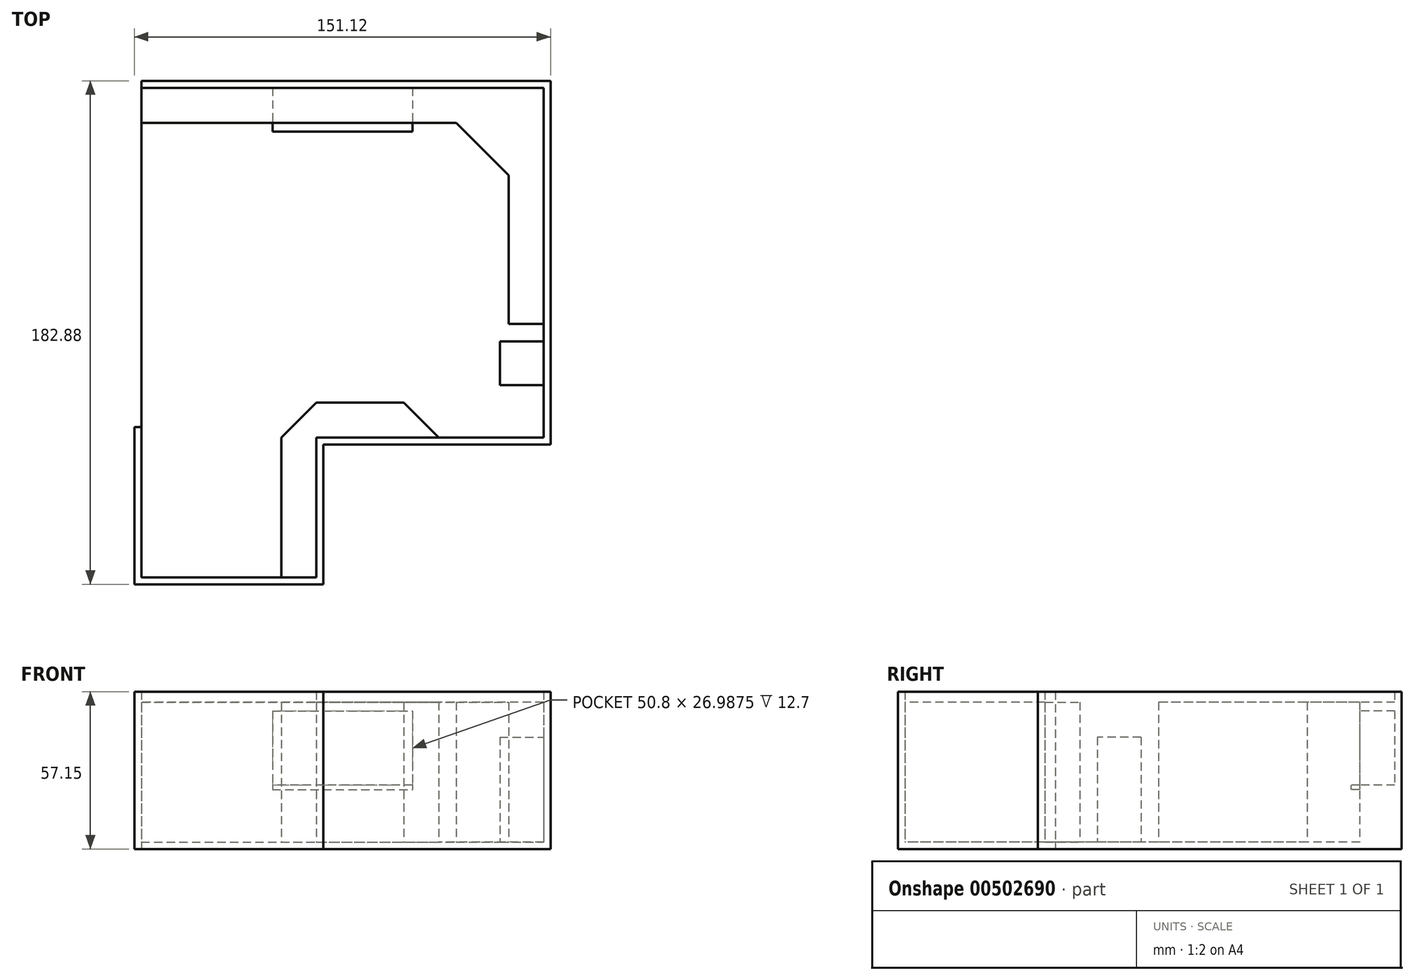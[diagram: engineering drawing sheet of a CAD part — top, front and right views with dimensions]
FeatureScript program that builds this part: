
annotation { "Feature Type Name" : "Feature", "Feature Type Description" : "" }
export const myFeature = defineFeature(function(context is Context, id is Id, definition is map)
    precondition{}
    {
        {
            var Q0;
            Q0=qCreatedBy(makeId("Top.planeOp"),FACE);
            var sketch = newSketch(context, id + "F0", { "sketchPlane" : qUnion([Q0])});
            skLineSegment(sketch, "E0.bottom", {"start": v(73.02, 63.5) * mm, "end": v(-73.03, 63.5) * mm});
            skLineSegment(sketch, "E0.top", {"start": v(73.03, -63.5) * mm, "end": v(-73.02, -63.5) * mm});
            skLineSegment(sketch, "E0.left", {"start": v(73.02, 63.5) * mm, "end": v(73.03, -63.5) * mm});
            skLineSegment(sketch, "E0.right", {"start": v(-73.03, 63.5) * mm, "end": v(-73.02, -63.5) * mm});
            skPoint(sketch, "E0.middle", {"position": v(0, 0) * mm});
            skSolve(sketch);
        }
        {
            var Q0;
            Q0=makeQuery(id+"F0.imprint","IMPRINT",FACE,{"disambiguationData":[TD([[makeQuery(id+"F0.imprint","IMPRINT",EDGE,{"derivedFrom":sQuery(id+"F0.wireOp",EDGE,"E0.bottom")}),1.0]])]});
            extrude(context, id + "F1", {"entities" : qUnion([Q0]), "depth" : 2.54 * mm});
        }
        {
            var Q0;
            Q0=makeQuery(id+"F1.opExtrude","CAP_FACE",FACE,{"disambiguationData":[OSD([sQuery(id+"F0.wireOp",EDGE,"E0.bottom"),sQuery(id+"F0.wireOp",EDGE,"E0.top"),sQuery(id+"F0.wireOp",EDGE,"E0.left"),sQuery(id+"F0.wireOp",EDGE,"E0.right")])],"isStart":false});
            var sketch = newSketch(context, id + "F2", { "sketchPlane" : qUnion([Q0])});
            skLineSegment(sketch, "E1.bottom", {"start": v(-73.03, 63.5) * mm, "end": v(73.03, 63.5) * mm});
            skLineSegment(sketch, "E1.top", {"start": v(-73.03, 50.8) * mm, "end": v(73.03, 50.8) * mm});
            skLineSegment(sketch, "E1.left", {"start": v(-73.03, 63.5) * mm, "end": v(-73.03, 50.8) * mm});
            skLineSegment(sketch, "E1.right", {"start": v(73.02, 63.5) * mm, "end": v(73.02, 50.8) * mm});
            skSolve(sketch);
        }
        {
            var Q0;
            Q0=makeQuery(id+"F2.imprint","IMPRINT",FACE,{"disambiguationData":[TD([[makeQuery(id+"F2.imprint","IMPRINT",EDGE,{"derivedFrom":sQuery(id+"F2.wireOp",EDGE,"E1.bottom")}),1.0]])]});
            extrude(context, id + "F3", {"entities" : qUnion([Q0]), "operationType" : NewBodyOperationType.ADD, "depth" : 50.8 * mm});
        }
        {
            var Q0;
            Q0=makeQuery(id+"F1.opExtrude","CAP_FACE",FACE,{"disambiguationData":[OSD([sQuery(id+"F0.wireOp",EDGE,"E0.bottom"),sQuery(id+"F0.wireOp",EDGE,"E0.top"),sQuery(id+"F0.wireOp",EDGE,"E0.left"),sQuery(id+"F0.wireOp",EDGE,"E0.right")])],"isStart":false});
            var sketch = newSketch(context, id + "F4", { "sketchPlane" : qUnion([Q0])});
            skLineSegment(sketch, "E2.bottom", {"start": v(57.15, -28.58) * mm, "end": v(73.03, -28.58) * mm});
            skLineSegment(sketch, "E2.top", {"start": v(57.15, -44.45) * mm, "end": v(73.03, -44.45) * mm});
            skLineSegment(sketch, "E2.left", {"start": v(57.15, -28.58) * mm, "end": v(57.15, -44.45) * mm});
            skLineSegment(sketch, "E2.right", {"start": v(73.03, -28.58) * mm, "end": v(73.03, -44.45) * mm});
            skSolve(sketch);
        }
        {
            var Q0;
            Q0=makeQuery(id+"F3.opExtrude","SWEPT_FACE",FACE,{"disambiguationData":[OSD([sQuery(id+"F2.wireOp",EDGE,"E1.top")])]});
            var sketch = newSketch(context, id + "F5", { "sketchPlane" : qUnion([Q0])});
            skLineSegment(sketch, "E3.bottom", {"start": v(-25.4, 50.17) * mm, "end": v(25.4, 50.17) * mm});
            skLineSegment(sketch, "E3.top", {"start": v(-25.4, 21.59) * mm, "end": v(25.4, 21.59) * mm});
            skLineSegment(sketch, "E3.left", {"start": v(-25.4, 50.17) * mm, "end": v(-25.4, 21.59) * mm});
            skLineSegment(sketch, "E3.right", {"start": v(25.4, 50.17) * mm, "end": v(25.4, 21.59) * mm});
            skSolve(sketch);
        }
        {
            var Q0;
            Q0=makeQuery(id+"F5.imprint","IMPRINT",FACE,{"disambiguationData":[TD([[makeQuery(id+"F5.imprint","IMPRINT",EDGE,{"derivedFrom":sQuery(id+"F5.wireOp",EDGE,"E3.bottom")}),-1.0]])]});
            extrude(context, id + "F6", {"entities" : qUnion([Q0]), "operationType" : NewBodyOperationType.REMOVE, "oppositeDirection" : true, "depth" : 12.7 * mm});
        }
        {
            var Q0;
            Q0=makeQuery(id+"F6.boolean.opBoolean","COPY",FACE,{"derivedFrom":makeQuery(id+"F6.opExtrude","SWEPT_FACE",FACE,{"disambiguationData":[OSD([sQuery(id+"F5.wireOp",EDGE,"E3.top")])]})});
            var sketch = newSketch(context, id + "F7", { "sketchPlane" : qUnion([Q0])});
            skLineSegment(sketch, "E4.bottom", {"start": v(25.4, 63.5) * mm, "end": v(-25.4, 63.5) * mm});
            skLineSegment(sketch, "E4.top", {"start": v(25.4, 47.63) * mm, "end": v(-25.4, 47.63) * mm});
            skLineSegment(sketch, "E4.left", {"start": v(25.4, 63.5) * mm, "end": v(25.4, 47.63) * mm});
            skLineSegment(sketch, "E4.right", {"start": v(-25.4, 63.5) * mm, "end": v(-25.4, 47.63) * mm});
            skSolve(sketch);
        }
        {
            var Q0;
            {var subQ0=sQuery(id+"F7.wireOp",EDGE,"E4.top");Q0=makeQuery(id+"F7.imprint","IMPRINT",FACE,{"disambiguationData":[TD([[makeQuery(id+"F7.imprint","IMPRINT",EDGE,{"derivedFrom":subQ0}),-1.0]])]});}
            var Q1;
            {var subQ0=sQuery(id+"F7.wireOp",EDGE,"E4.bottom");Q1=makeQuery(id+"F7.imprint","IMPRINT",FACE,{"disambiguationData":[TD([[makeQuery(id+"F7.imprint","IMPRINT",EDGE,{"derivedFrom":subQ0}),-1.0]])]});}
            extrude(context, id + "F8", {"entities" : qUnion([Q0, Q1]), "operationType" : NewBodyOperationType.ADD, "depth" : 1.59 * mm});
        }
        {
            var Q0;
            Q0=qCreatedBy(makeId("Top.planeOp"),FACE);
            var sketch = newSketch(context, id + "F9", { "sketchPlane" : qUnion([Q0])});
            skLineSegment(sketch, "E5.bottom", {"start": v(-73.02, -63.5) * mm, "end": v(-9.52, -63.5) * mm});
            skLineSegment(sketch, "E5.top", {"start": v(-73.02, -114.3) * mm, "end": v(-9.52, -114.3) * mm});
            skLineSegment(sketch, "E5.left", {"start": v(-73.02, -63.5) * mm, "end": v(-73.02, -114.3) * mm});
            skLineSegment(sketch, "E5.right", {"start": v(-9.52, -63.5) * mm, "end": v(-9.52, -114.3) * mm});
            skSolve(sketch);
        }
        {
            var Q0;
            Q0=makeQuery(id+"F9.imprint","IMPRINT",FACE,{"disambiguationData":[TD([[makeQuery(id+"F9.imprint","IMPRINT",EDGE,{"derivedFrom":sQuery(id+"F9.wireOp",EDGE,"E5.bottom")}),-1.0]])]});
            extrude(context, id + "F10", {"entities" : qUnion([Q0]), "operationType" : NewBodyOperationType.ADD, "depth" : 2.54 * mm});
        }
        {
            var Q0;
            Q0=makeQuery(id+"F10.boolean.opBoolean","MERGE",FACE,{"derivedFrom":[makeQuery(id+"F1.opExtrude","CAP_FACE",FACE,{"disambiguationData":[OSD([sQuery(id+"F0.wireOp",EDGE,"E0.bottom"),sQuery(id+"F0.wireOp",EDGE,"E0.top"),sQuery(id+"F0.wireOp",EDGE,"E0.left"),sQuery(id+"F0.wireOp",EDGE,"E0.right")])],"isStart":false}),makeQuery(id+"F10.opExtrude","CAP_FACE",FACE,{"disambiguationData":[OSD([sQuery(id+"F9.wireOp",EDGE,"E5.bottom"),sQuery(id+"F9.wireOp",EDGE,"E5.top"),sQuery(id+"F9.wireOp",EDGE,"E5.left"),sQuery(id+"F9.wireOp",EDGE,"E5.right")])],"isStart":false})]});
            var sketch = newSketch(context, id + "F11", { "sketchPlane" : qUnion([Q0])});
            skLineSegment(sketch, "E6.bottom", {"start": v(73.02, 50.8) * mm, "end": v(60.32, 50.8) * mm});
            skLineSegment(sketch, "E6.top", {"start": v(73.02, -22.23) * mm, "end": v(60.33, -22.23) * mm});
            skLineSegment(sketch, "E6.left", {"start": v(73.02, 50.8) * mm, "end": v(73.02, -22.23) * mm});
            skLineSegment(sketch, "E6.right", {"start": v(60.32, 50.8) * mm, "end": v(60.33, -22.23) * mm});
            skSolve(sketch);
        }
        {
            var Q0;
            Q0 = qSketchRegion(id + "F11", true);
            extrude(context, id + "F12", {"entities" : qUnion([Q0]), "operationType" : NewBodyOperationType.ADD, "depth" : 50.8 * mm});
        }
        {
            var Q0;
            Q0=qCreatedBy(makeId("Top.planeOp"),FACE);
            var sketch = newSketch(context, id + "F13", { "sketchPlane" : qUnion([Q0])});
            skLineSegment(sketch, "E7.bottom", {"start": v(-73.03, 63.5) * mm, "end": v(75.57, 63.5) * mm});
            skLineSegment(sketch, "E7.top", {"start": v(-73.03, 66.04) * mm, "end": v(75.57, 66.04) * mm});
            skLineSegment(sketch, "E7.left", {"start": v(-73.03, 63.5) * mm, "end": v(-73.03, 66.04) * mm});
            skLineSegment(sketch, "E7.right", {"start": v(75.57, 63.5) * mm, "end": v(75.57, 66.04) * mm});
            skSolve(sketch);
        }
        {
            var Q0;
            Q0=qCreatedBy(makeId("Top.planeOp"),FACE);
            var sketch = newSketch(context, id + "F14", { "sketchPlane" : qUnion([Q0])});
            skLineSegment(sketch, "E8.bottom", {"start": v(73.03, 63.5) * mm, "end": v(75.57, 63.5) * mm});
            skLineSegment(sketch, "E8.top", {"start": v(73.03, -63.5) * mm, "end": v(75.57, -63.5) * mm});
            skLineSegment(sketch, "E8.left", {"start": v(73.02, 63.5) * mm, "end": v(73.03, -63.5) * mm});
            skLineSegment(sketch, "E8.right", {"start": v(75.57, 63.5) * mm, "end": v(75.57, -63.5) * mm});
            skSolve(sketch);
        }
        {
            var Q0;
            Q0=makeQuery(id+"F13.imprint","IMPRINT",FACE,{"disambiguationData":[TD([[makeQuery(id+"F13.imprint","IMPRINT",EDGE,{"derivedFrom":sQuery(id+"F13.wireOp",EDGE,"E7.bottom")}),1.0]])]});
            extrude(context, id + "F15", {"entities" : qUnion([Q0]), "operationType" : NewBodyOperationType.ADD, "depth" : 57.15 * mm});
        }
        {
            var Q0;
            Q0=makeQuery(id+"F14.imprint","IMPRINT",FACE,{"disambiguationData":[TD([[makeQuery(id+"F14.imprint","IMPRINT",EDGE,{"derivedFrom":sQuery(id+"F14.wireOp",EDGE,"E8.bottom")}),-1.0]])]});
            extrude(context, id + "F16", {"entities" : qUnion([Q0]), "operationType" : NewBodyOperationType.ADD, "depth" : 57.15 * mm});
        }
        {
            var Q0;
            Q0=makeQuery(id+"F10.boolean.opBoolean","MERGE",FACE,{"derivedFrom":[makeQuery(id+"F1.opExtrude","CAP_FACE",FACE,{"disambiguationData":[OSD([sQuery(id+"F0.wireOp",EDGE,"E0.bottom"),sQuery(id+"F0.wireOp",EDGE,"E0.top"),sQuery(id+"F0.wireOp",EDGE,"E0.left"),sQuery(id+"F0.wireOp",EDGE,"E0.right")])],"isStart":false}),makeQuery(id+"F10.opExtrude","CAP_FACE",FACE,{"disambiguationData":[OSD([sQuery(id+"F9.wireOp",EDGE,"E5.bottom"),sQuery(id+"F9.wireOp",EDGE,"E5.top"),sQuery(id+"F9.wireOp",EDGE,"E5.left"),sQuery(id+"F9.wireOp",EDGE,"E5.right")])],"isStart":false})]});
            var sketch = newSketch(context, id + "F17", { "sketchPlane" : qUnion([Q0])});
            skLineSegment(sketch, "E9", {"start": v(60.32, 50.8) * mm, "end": v(41.28, 50.8) * mm});
            skLineSegment(sketch, "E10", {"start": v(41.28, 50.8) * mm, "end": v(60.32, 31.75) * mm});
            skLineSegment(sketch, "E11", {"start": v(60.33, 31.75) * mm, "end": v(60.33, 50.8) * mm});
            skSolve(sketch);
        }
        {
            var Q0;
            Q0=makeQuery(id+"F17.imprint","IMPRINT",FACE,{"disambiguationData":[TD([[makeQuery(id+"F17.imprint","IMPRINT",EDGE,{"derivedFrom":sQuery(id+"F17.wireOp",EDGE,"E9")}),-1.0]])]});
            extrude(context, id + "F18", {"entities" : qUnion([Q0]), "operationType" : NewBodyOperationType.ADD, "depth" : 50.8 * mm});
        }
        {
            var Q0;
            Q0=makeQuery(id+"F10.boolean.opBoolean","MERGE",FACE,{"derivedFrom":[makeQuery(id+"F1.opExtrude","CAP_FACE",FACE,{"disambiguationData":[OSD([sQuery(id+"F0.wireOp",EDGE,"E0.bottom"),sQuery(id+"F0.wireOp",EDGE,"E0.top"),sQuery(id+"F0.wireOp",EDGE,"E0.left"),sQuery(id+"F0.wireOp",EDGE,"E0.right")])],"isStart":false}),makeQuery(id+"F10.opExtrude","CAP_FACE",FACE,{"disambiguationData":[OSD([sQuery(id+"F9.wireOp",EDGE,"E5.bottom"),sQuery(id+"F9.wireOp",EDGE,"E5.top"),sQuery(id+"F9.wireOp",EDGE,"E5.left"),sQuery(id+"F9.wireOp",EDGE,"E5.right")])],"isStart":false})]});
            var sketch = newSketch(context, id + "F19", { "sketchPlane" : qUnion([Q0])});
            skLineSegment(sketch, "E12.bottom", {"start": v(-9.52, -63.5) * mm, "end": v(22.23, -63.5) * mm});
            skLineSegment(sketch, "E12.top", {"start": v(-9.52, -50.8) * mm, "end": v(22.23, -50.8) * mm});
            skLineSegment(sketch, "E12.left", {"start": v(-9.52, -63.5) * mm, "end": v(-9.52, -50.8) * mm});
            skLineSegment(sketch, "E12.right", {"start": v(22.23, -63.5) * mm, "end": v(22.23, -50.8) * mm});
            skSolve(sketch);
        }
        {
            var Q0;
            Q0=makeQuery(id+"F19.imprint","IMPRINT",FACE,{"disambiguationData":[TD([[makeQuery(id+"F19.imprint","IMPRINT",EDGE,{"derivedFrom":sQuery(id+"F19.wireOp",EDGE,"E12.bottom")}),-1.0]])]});
            extrude(context, id + "F20", {"entities" : qUnion([Q0]), "operationType" : NewBodyOperationType.ADD, "depth" : 50.8 * mm});
        }
        {
            var Q0;
            Q0=makeQuery(id+"F10.boolean.opBoolean","MERGE",FACE,{"derivedFrom":[makeQuery(id+"F1.opExtrude","CAP_FACE",FACE,{"disambiguationData":[OSD([sQuery(id+"F0.wireOp",EDGE,"E0.bottom"),sQuery(id+"F0.wireOp",EDGE,"E0.top"),sQuery(id+"F0.wireOp",EDGE,"E0.left"),sQuery(id+"F0.wireOp",EDGE,"E0.right")])],"isStart":false}),makeQuery(id+"F10.opExtrude","CAP_FACE",FACE,{"disambiguationData":[OSD([sQuery(id+"F9.wireOp",EDGE,"E5.bottom"),sQuery(id+"F9.wireOp",EDGE,"E5.top"),sQuery(id+"F9.wireOp",EDGE,"E5.left"),sQuery(id+"F9.wireOp",EDGE,"E5.right")])],"isStart":false})]});
            var sketch = newSketch(context, id + "F21", { "sketchPlane" : qUnion([Q0])});
            skLineSegment(sketch, "E13", {"start": v(22.23, -50.8) * mm, "end": v(34.93, -63.5) * mm});
            skLineSegment(sketch, "E14", {"start": v(34.93, -63.5) * mm, "end": v(22.23, -63.5) * mm});
            skLineSegment(sketch, "E15", {"start": v(22.23, -63.5) * mm, "end": v(22.23, -50.8) * mm});
            skSolve(sketch);
        }
        {
            var Q0;
            Q0=makeQuery(id+"F21.imprint","IMPRINT",FACE,{"disambiguationData":[TD([[makeQuery(id+"F21.imprint","IMPRINT",EDGE,{"derivedFrom":sQuery(id+"F21.wireOp",EDGE,"E13")}),-1.0]])]});
            extrude(context, id + "F22", {"entities" : qUnion([Q0]), "operationType" : NewBodyOperationType.ADD, "depth" : 50.8 * mm});
        }
        {
            var Q0;
            Q0=makeQuery(id+"F10.boolean.opBoolean","MERGE",FACE,{"derivedFrom":[makeQuery(id+"F1.opExtrude","CAP_FACE",FACE,{"disambiguationData":[OSD([sQuery(id+"F0.wireOp",EDGE,"E0.bottom"),sQuery(id+"F0.wireOp",EDGE,"E0.top"),sQuery(id+"F0.wireOp",EDGE,"E0.left"),sQuery(id+"F0.wireOp",EDGE,"E0.right")])],"isStart":false}),makeQuery(id+"F10.opExtrude","CAP_FACE",FACE,{"disambiguationData":[OSD([sQuery(id+"F9.wireOp",EDGE,"E5.bottom"),sQuery(id+"F9.wireOp",EDGE,"E5.top"),sQuery(id+"F9.wireOp",EDGE,"E5.left"),sQuery(id+"F9.wireOp",EDGE,"E5.right")])],"isStart":false})]});
            var sketch = newSketch(context, id + "F23", { "sketchPlane" : qUnion([Q0])});
            skLineSegment(sketch, "E16", {"start": v(-9.52, -50.8) * mm, "end": v(-9.52, -63.5) * mm});
            skLineSegment(sketch, "E17", {"start": v(-9.52, -63.5) * mm, "end": v(-22.21, -63.5) * mm});
            skLineSegment(sketch, "E18", {"start": v(-22.21, -63.5) * mm, "end": v(-9.52, -50.8) * mm});
            skSolve(sketch);
        }
        {
            var Q0;
            Q0=makeQuery(id+"F23.imprint","IMPRINT",FACE,{"disambiguationData":[TD([[makeQuery(id+"F23.imprint","IMPRINT",EDGE,{"derivedFrom":sQuery(id+"F23.wireOp",EDGE,"E16")}),1.0]])]});
            extrude(context, id + "F24", {"entities" : qUnion([Q0]), "operationType" : NewBodyOperationType.ADD, "depth" : 50.8 * mm});
        }
        {
            var Q0;
            Q0=makeQuery(id+"F10.boolean.opBoolean","MERGE",FACE,{"derivedFrom":[makeQuery(id+"F1.opExtrude","CAP_FACE",FACE,{"disambiguationData":[OSD([sQuery(id+"F0.wireOp",EDGE,"E0.bottom"),sQuery(id+"F0.wireOp",EDGE,"E0.top"),sQuery(id+"F0.wireOp",EDGE,"E0.left"),sQuery(id+"F0.wireOp",EDGE,"E0.right")])],"isStart":false}),makeQuery(id+"F10.opExtrude","CAP_FACE",FACE,{"disambiguationData":[OSD([sQuery(id+"F9.wireOp",EDGE,"E5.bottom"),sQuery(id+"F9.wireOp",EDGE,"E5.top"),sQuery(id+"F9.wireOp",EDGE,"E5.left"),sQuery(id+"F9.wireOp",EDGE,"E5.right")])],"isStart":false})]});
            var sketch = newSketch(context, id + "F25", { "sketchPlane" : qUnion([Q0])});
            skLineSegment(sketch, "E19.bottom", {"start": v(-22.21, -63.5) * mm, "end": v(-9.52, -63.5) * mm});
            skLineSegment(sketch, "E19.top", {"start": v(-22.21, -114.3) * mm, "end": v(-9.52, -114.3) * mm});
            skLineSegment(sketch, "E19.left", {"start": v(-22.21, -63.5) * mm, "end": v(-22.21, -114.3) * mm});
            skLineSegment(sketch, "E19.right", {"start": v(-9.52, -63.5) * mm, "end": v(-9.52, -114.3) * mm});
            skSolve(sketch);
        }
        {
            var Q0;
            Q0=makeQuery(id+"F25.imprint","IMPRINT",FACE,{"disambiguationData":[TD([[makeQuery(id+"F25.imprint","IMPRINT",EDGE,{"derivedFrom":sQuery(id+"F25.wireOp",EDGE,"E19.bottom")}),1.0]])]});
            extrude(context, id + "F26", {"entities" : qUnion([Q0]), "operationType" : NewBodyOperationType.ADD, "depth" : 50.8 * mm});
        }
        {
            var Q0;
            Q0=makeQuery(id+"F4.imprint","IMPRINT",FACE,{"disambiguationData":[TD([[makeQuery(id+"F4.imprint","IMPRINT",EDGE,{"derivedFrom":sQuery(id+"F4.wireOp",EDGE,"E2.bottom")}),-1.0]])]});
            extrude(context, id + "F27", {"entities" : qUnion([Q0]), "operationType" : NewBodyOperationType.ADD, "depth" : 38.1 * mm});
        }
        {
            var Q0;
            Q0=qCreatedBy(makeId("Top.planeOp"),FACE);
            var sketch = newSketch(context, id + "F28", { "sketchPlane" : qUnion([Q0])});
            skLineSegment(sketch, "E20.bottom", {"start": v(-9.52, -63.5) * mm, "end": v(75.57, -63.5) * mm});
            skLineSegment(sketch, "E20.top", {"start": v(-9.52, -66.04) * mm, "end": v(75.57, -66.04) * mm});
            skLineSegment(sketch, "E20.left", {"start": v(-9.52, -63.5) * mm, "end": v(-9.52, -66.04) * mm});
            skLineSegment(sketch, "E20.right", {"start": v(75.57, -63.5) * mm, "end": v(75.57, -66.04) * mm});
            skSolve(sketch);
        }
        {
            var Q0;
            Q0=makeQuery(id+"F28.imprint","IMPRINT",FACE,{"disambiguationData":[TD([[makeQuery(id+"F28.imprint","IMPRINT",EDGE,{"derivedFrom":sQuery(id+"F28.wireOp",EDGE,"E20.bottom")}),-1.0]])]});
            extrude(context, id + "F29", {"entities" : qUnion([Q0]), "operationType" : NewBodyOperationType.ADD, "depth" : 57.15 * mm});
        }
        {
            var Q0;
            Q0=qCreatedBy(makeId("Top.planeOp"),FACE);
            var sketch = newSketch(context, id + "F30", { "sketchPlane" : qUnion([Q0])});
            skLineSegment(sketch, "E21.bottom", {"start": v(-9.52, -66.04) * mm, "end": v(-6.98, -66.04) * mm});
            skLineSegment(sketch, "E21.top", {"start": v(-9.52, -116.84) * mm, "end": v(-6.98, -116.84) * mm});
            skLineSegment(sketch, "E21.left", {"start": v(-9.52, -66.04) * mm, "end": v(-9.52, -116.84) * mm});
            skLineSegment(sketch, "E21.right", {"start": v(-6.98, -66.04) * mm, "end": v(-6.98, -116.84) * mm});
            skSolve(sketch);
        }
        {
            var Q0;
            Q0=qCreatedBy(makeId("Top.planeOp"),FACE);
            var sketch = newSketch(context, id + "F31", { "sketchPlane" : qUnion([Q0])});
            skLineSegment(sketch, "E22.bottom", {"start": v(-73.02, -114.3) * mm, "end": v(-9.52, -114.3) * mm});
            skLineSegment(sketch, "E22.top", {"start": v(-73.02, -116.84) * mm, "end": v(-9.52, -116.84) * mm});
            skLineSegment(sketch, "E22.left", {"start": v(-73.02, -114.3) * mm, "end": v(-73.02, -116.84) * mm});
            skLineSegment(sketch, "E22.right", {"start": v(-9.52, -114.3) * mm, "end": v(-9.52, -116.84) * mm});
            skSolve(sketch);
        }
        {
            var Q0;
            Q0=makeQuery(id+"F30.imprint","IMPRINT",FACE,{"disambiguationData":[TD([[makeQuery(id+"F30.imprint","IMPRINT",EDGE,{"derivedFrom":sQuery(id+"F30.wireOp",EDGE,"E21.bottom")}),-1.0]])]});
            extrude(context, id + "F32", {"entities" : qUnion([Q0]), "operationType" : NewBodyOperationType.ADD, "depth" : 57.15 * mm});
        }
        {
            var Q0;
            Q0=makeQuery(id+"F31.imprint","IMPRINT",FACE,{"disambiguationData":[TD([[makeQuery(id+"F31.imprint","IMPRINT",EDGE,{"derivedFrom":sQuery(id+"F31.wireOp",EDGE,"E22.bottom")}),-1.0]])]});
            extrude(context, id + "F33", {"entities" : qUnion([Q0]), "operationType" : NewBodyOperationType.ADD, "depth" : 57.15 * mm});
        }
        {
            var Q0;
            Q0=qCreatedBy(makeId("Top.planeOp"),FACE);
            var sketch = newSketch(context, id + "F34", { "sketchPlane" : qUnion([Q0])});
            skLineSegment(sketch, "E23.bottom", {"start": v(-73.02, -116.84) * mm, "end": v(-75.56, -116.84) * mm});
            skLineSegment(sketch, "E23.top", {"start": v(-73.02, -59.7) * mm, "end": v(-75.57, -59.7) * mm});
            skLineSegment(sketch, "E23.left", {"start": v(-73.02, -116.84) * mm, "end": v(-73.02, -59.7) * mm});
            skLineSegment(sketch, "E23.right", {"start": v(-75.56, -116.84) * mm, "end": v(-75.57, -59.7) * mm});
            skSolve(sketch);
        }
        {
            var Q0;
            Q0=makeQuery(id+"F34.imprint","IMPRINT",FACE,{"disambiguationData":[TD([[makeQuery(id+"F34.imprint","IMPRINT",EDGE,{"derivedFrom":sQuery(id+"F34.wireOp",EDGE,"E23.bottom")}),-1.0]])]});
            extrude(context, id + "F35", {"entities" : qUnion([Q0]), "operationType" : NewBodyOperationType.ADD, "depth" : 57.15 * mm});
        }
    });
